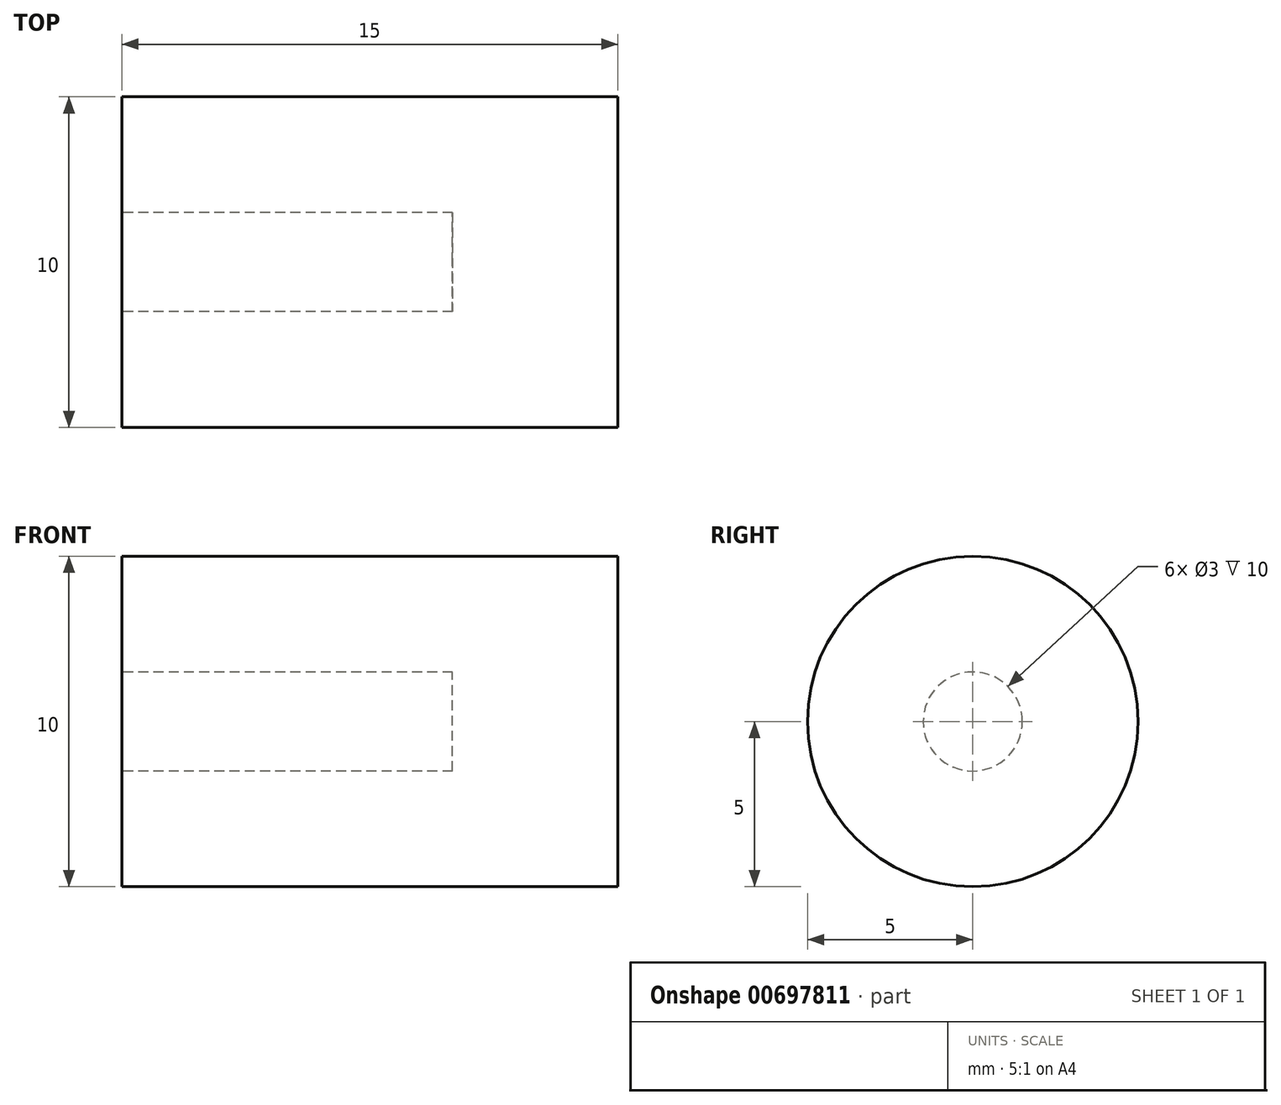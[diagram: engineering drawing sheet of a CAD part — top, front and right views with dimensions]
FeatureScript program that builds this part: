
annotation { "Feature Type Name" : "Feature", "Feature Type Description" : "" }
export const myFeature = defineFeature(function(context is Context, id is Id, definition is map)
    precondition{}
    {
        {
            var Q0;
            Q0=qCreatedBy(makeId("Right.planeOp"),FACE);
            var sketch = newSketch(context, id + "F0", { "sketchPlane" : qUnion([Q0])});
            skCircle(sketch, "E0", {"center": v(0, 0) * mm, "radius": 5 * mm});
            skCircle(sketch, "E1", {"center": v(0, 0) * mm, "radius": 1.5 * mm});
            skSolve(sketch);
        }
        {
            var Q0;
            Q0=qSketchRegion(id+"F0",true);
            var Q1;
            Q1=makeQuery(id+"F0.imprint","IMPRINT",FACE,{"disambiguationData":[TD([[makeQuery(id+"F0.imprint","IMPRINT",EDGE,{"derivedFrom":sQuery(id+"F0.wireOp",EDGE,"E1")}),1.0]])]});
            extrude(context, id + "F1", {"entities" : qUnion([Q0, Q1]), "depth" : 15 * mm, "offsetDistance" : 25 * mm});
        }
        {
            var Q0;
            Q0=makeQuery(id+"F0.imprint","IMPRINT",FACE,{"disambiguationData":[TD([[makeQuery(id+"F0.imprint","IMPRINT",EDGE,{"derivedFrom":sQuery(id+"F0.wireOp",EDGE,"E1")}),1.0]])]});
            var Q1;
            Q1=sQuery(id+"F0.wireOp",EDGE,"E1");
            extrude(context, id + "F2", {"entities" : qUnion([Q0]), "operationType" : NewBodyOperationType.REMOVE, "surfaceEntities" : qUnion([Q1]), "depth" : 10 * mm, "offsetDistance" : 25 * mm});
        }
    });
